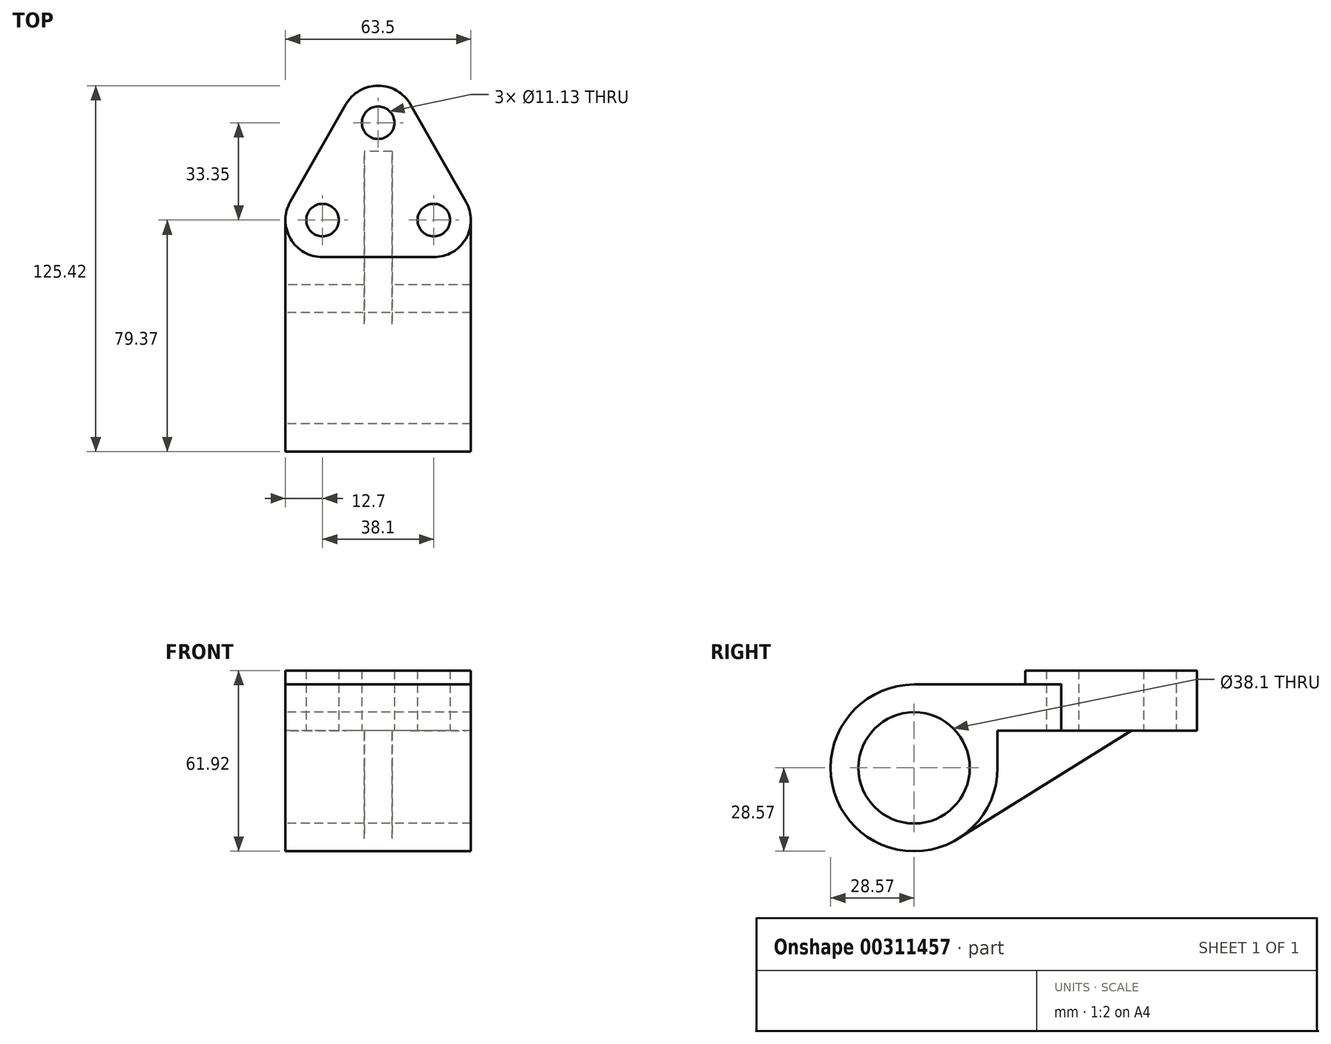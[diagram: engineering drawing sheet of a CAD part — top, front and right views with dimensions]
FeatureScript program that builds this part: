
annotation { "Feature Type Name" : "Feature", "Feature Type Description" : "" }
export const myFeature = defineFeature(function(context is Context, id is Id, definition is map)
    precondition{}
    {
        {
            var Q0;
            Q0=qCreatedBy(makeId("Top.planeOp"),FACE);
            var sketch = newSketch(context, id + "F0", { "sketchPlane" : qUnion([Q0])});
            skLineSegment(sketch, "E0", {"start": v(-11.03, 19) * mm, "end": v(8.02, 52.35) * mm});
            skLineSegment(sketch, "E1", {"start": v(30.08, 52.35) * mm, "end": v(49.13, 19) * mm});
            skLineSegment(sketch, "E2", {"start": v(38.1, 0) * mm, "end": v(0, 0) * mm});
            skArc(sketch, "E3.filletArc", {"start": v(-11.03, 19) * mm, "mid": v(-10.98, 6.32) * mm, "end": v(0, 0) * mm});
            skPoint(sketch, "E4.visualSharp", {"position": v(19.05, 71.66) * mm});
            skArc(sketch, "E4.filletArc", {"start": v(30.08, 52.35) * mm, "mid": v(19.05, 58.75) * mm, "end": v(8.02, 52.35) * mm});
            skPoint(sketch, "E5.visualSharp", {"position": v(59.98, 0) * mm});
            skArc(sketch, "E5.filletArc", {"start": v(38.1, 0) * mm, "mid": v(49.08, 6.32) * mm, "end": v(49.13, 19) * mm});
            skCircle(sketch, "E6", {"center": v(0, 12.7) * mm, "radius": 5.56 * mm});
            skCircle(sketch, "E7", {"center": v(19.05, 46.05) * mm, "radius": 5.56 * mm});
            skCircle(sketch, "E8", {"center": v(38.1, 12.7) * mm, "radius": 5.56 * mm});
            skSolve(sketch);
        }
        {
            var Q0;
            Q0 = qSketchRegion(id + "F0", true);
            extrude(context, id + "F1", {"entities" : qUnion([Q0]), "depth" : 20.65 * mm});
        }
        {
            var Q0;
            Q0=qCreatedBy(makeId("Top.planeOp"),FACE);
            var sketch = newSketch(context, id + "F2", { "sketchPlane" : qUnion([Q0])});
            skPoint(sketch, "E9.0", {"position": v(0, 12.7) * mm});
            skArc(sketch, "E10.0", {"start": v(-11.03, 19) * mm, "mid": v(-10.98, 6.32) * mm, "end": v(0, 0) * mm});
            skLineSegment(sketch, "E11.bottom", {"start": v(-12.7, 12.7) * mm, "end": v(50.8, 12.7) * mm});
            skLineSegment(sketch, "E11.top", {"start": v(-12.7, -38.1) * mm, "end": v(50.8, -38.1) * mm});
            skLineSegment(sketch, "E11.left", {"start": v(-12.7, 12.7) * mm, "end": v(-12.7, -38.1) * mm});
            skLineSegment(sketch, "E11.right", {"start": v(50.8, 12.7) * mm, "end": v(50.8, -38.1) * mm});
            skSolve(sketch);
        }
        {
            var Q0;
            Q0 = qSketchRegion(id + "F2", true);
            extrude(context, id + "F3", {"entities" : qUnion([Q0]), "operationType" : NewBodyOperationType.ADD, "depth" : 15.88 * mm});
        }
        {
            var Q0;
            Q0=makeQuery(id+"F0.imprint","IMPRINT",FACE,{"disambiguationData":[TD([[makeQuery(id+"F0.imprint","IMPRINT",EDGE,{"derivedFrom":sQuery(id+"F0.wireOp",EDGE,"E6")}),1.0]])]});
            var Q1;
            Q1=makeQuery(id+"F0.imprint","IMPRINT",FACE,{"disambiguationData":[TD([[makeQuery(id+"F0.imprint","IMPRINT",EDGE,{"derivedFrom":sQuery(id+"F0.wireOp",EDGE,"E8")}),1.0]])]});
            extrude(context, id + "F4", {"entities" : qUnion([Q0, Q1]), "operationType" : NewBodyOperationType.REMOVE, "endBound" : BoundingType.THROUGH_ALL, "depth" : 25.4 * mm});
        }
        {
            var Q0;
            Q0=qCreatedBy(makeId("Right.planeOp"),FACE);
            var sketch = newSketch(context, id + "F5", { "sketchPlane" : qUnion([Q0])});
            skArc(sketch, "E12", {"start": v(-38.1, 15.88) * mm, "mid": v(-58.3, -32.9) * mm, "end": v(-9.53, -12.7) * mm});
            skCircle(sketch, "E13", {"center": v(-38.1, -12.7) * mm, "radius": 19.05 * mm});
            skPoint(sketch, "E14.0", {"position": v(-38.1, 15.88) * mm});
            skLineSegment(sketch, "E15", {"start": v(-9.53, -12.7) * mm, "end": v(-9.53, 0) * mm});
            skLineSegment(sketch, "E16.0.0", {"start": v(12.29, 0) * mm, "end": v(12.29, 15.88) * mm});
            skLineSegment(sketch, "E16.0.1", {"start": v(12.29, 15.88) * mm, "end": v(-38.1, 15.88) * mm});
            skLineSegment(sketch, "E16.0.2", {"start": v(-38.1, 15.88) * mm, "end": v(-38.1, 6.35) * mm});
            skLineSegment(sketch, "E16.0.3", {"start": v(-23.9, 0) * mm, "end": v(-9.53, 0) * mm});
            skPoint(sketch, "E17.orphan", {"position": v(-38.1, 0) * mm});
            skLineSegment(sketch, "E18", {"start": v(-9.53, 0) * mm, "end": v(36.3, 0) * mm});
            skLineSegment(sketch, "E19", {"start": v(36.3, 0) * mm, "end": v(-22.98, -36.95) * mm});
            skSolve(sketch);
        }
        {
            var Q0;
            Q0=makeQuery(id+"F5.imprint","IMPRINT",FACE,{"disambiguationData":[TD([[makeQuery(id+"F5.imprint","IMPRINT",EDGE,{"derivedFrom":sQuery(id+"F5.wireOp",EDGE,"E12")}),1.0]])]});
            var Q1;
            Q1=makeQuery(id+"F3.opExtrude","SWEPT_FACE",FACE,{"disambiguationData":[OSD([sQuery(id+"F2.wireOp",EDGE,"E11.right")])]});
            var Q2;
            Q2=makeQuery(id+"F3.opExtrude","SWEPT_FACE",FACE,{"disambiguationData":[OSD([sQuery(id+"F2.wireOp",EDGE,"E11.left")])]});
            extrude(context, id + "F6", {"entities" : qUnion([Q0]), "operationType" : NewBodyOperationType.ADD, "endBound" : BoundingType.UP_TO_SURFACE, "endBoundEntityFace" : qUnion([Q1]), "depth" : 49.78 * mm, "hasSecondDirection" : true, "secondDirectionBound" : SecondDirectionBoundingType.UP_TO_SURFACE, "secondDirectionOppositeDirection" : true, "secondDirectionBoundEntityFace" : qUnion([Q2]), "secondDirectionDepth" : 25.4 * mm});
        }
        {
            var Q0;
            {var subQ0=sQuery(id+"F5.wireOp",EDGE,"E13");var subQ1=makeQuery(id+"F5.imprint","INTERSECT",VERTEX,{"derivedFrom":[subQ0,sQuery(id+"F5.wireOp",EDGE,"E16.0.2")]});Q0=makeQuery(id+"F5.imprint","IMPRINT",FACE,{"disambiguationData":[TD([[makeQuery(id+"F5.imprint","IMPRINT",EDGE,{"disambiguationData":[TD([[subQ1,1.0]])],"derivedFrom":subQ0}),1.0]])]});}
            extrude(context, id + "F7", {"entities" : qUnion([Q0]), "operationType" : NewBodyOperationType.REMOVE, "endBound" : BoundingType.THROUGH_ALL, "oppositeDirection" : true, "depth" : 25.4 * mm, "hasSecondDirection" : true, "secondDirectionBound" : SecondDirectionBoundingType.THROUGH_ALL, "secondDirectionOppositeDirection" : false, "secondDirectionDepth" : 25.4 * mm});
        }
        {
            var Q0;
            {var subQ3=sQuery(id+"F5.wireOp",EDGE,"E15");Q0=makeQuery(id+"F5.imprint","IMPRINT",FACE,{"disambiguationData":[TD([[makeQuery(id+"F5.imprint","IMPRINT",EDGE,{"derivedFrom":subQ3}),-1.0]])]});}
            extrude(context, id + "F8", {"entities" : qUnion([Q0]), "operationType" : NewBodyOperationType.ADD, "depth" : 23.8 * mm});
        }
        {
            var Q0;
            {var subQ3=sQuery(id+"F5.wireOp",EDGE,"E15");Q0=makeQuery(id+"F5.imprint","IMPRINT",FACE,{"disambiguationData":[TD([[makeQuery(id+"F5.imprint","IMPRINT",EDGE,{"derivedFrom":subQ3}),-1.0]])]});}
            extrude(context, id + "F9", {"entities" : qUnion([Q0]), "operationType" : NewBodyOperationType.REMOVE, "depth" : 14.29 * mm});
        }
    });
